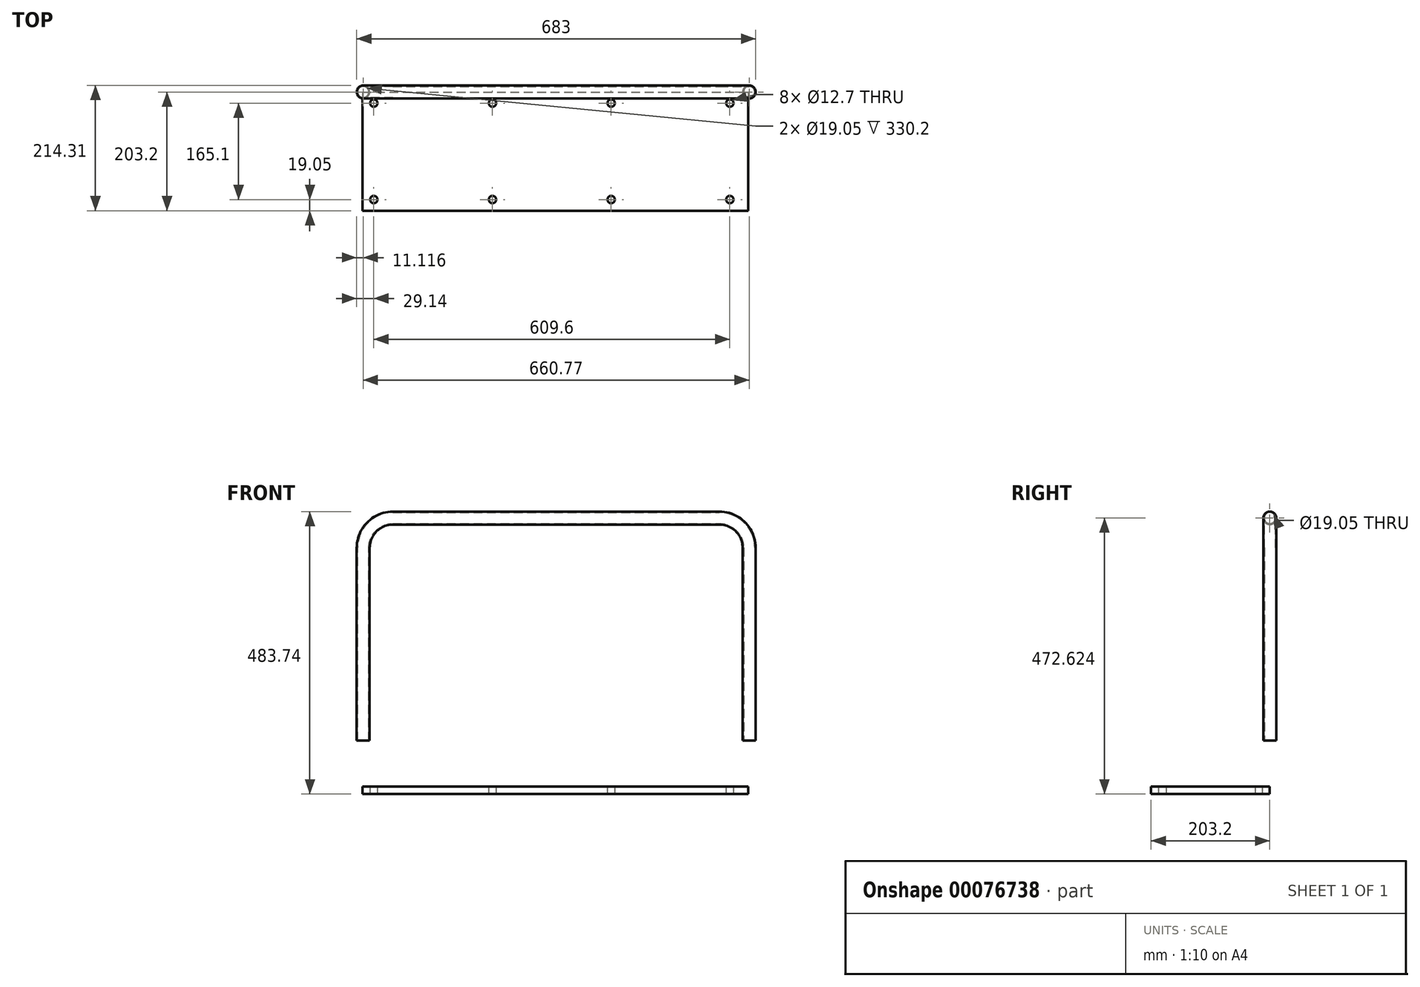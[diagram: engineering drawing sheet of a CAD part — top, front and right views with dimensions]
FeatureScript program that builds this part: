
annotation { "Feature Type Name" : "Feature", "Feature Type Description" : "" }
export const myFeature = defineFeature(function(context is Context, id is Id, definition is map)
    precondition{}
    {
        {
            var Q0;
            Q0=qCreatedBy(makeId("Top.planeOp"),FACE);
            var sketch = newSketch(context, id + "F0", { "sketchPlane" : qUnion([Q0])});
            skLineSegment(sketch, "E0.bottom", {"start": v(-330.2, 0) * mm, "end": v(330.2, 0) * mm});
            skLineSegment(sketch, "E0.top", {"start": v(-330.2, -203.2) * mm, "end": v(330.2, -203.2) * mm});
            skLineSegment(sketch, "E0.left", {"start": v(-330.2, 0) * mm, "end": v(-330.2, -203.2) * mm});
            skLineSegment(sketch, "E0.right", {"start": v(330.2, 0) * mm, "end": v(330.2, -203.2) * mm});
            skSolve(sketch);
        }
        {
            var Q0;
            Q0=makeQuery(id+"F0.imprint","IMPRINT",FACE,{"disambiguationData":[TD([[makeQuery(id+"F0.imprint","IMPRINT",EDGE,{"derivedFrom":sQuery(id+"F0.wireOp",EDGE,"E0.bottom")}),-1.0]])]});
            var sketch = newSketch(context, id + "F1", { "sketchPlane" : qUnion([Q0])});
            skCircle(sketch, "E1", {"center": v(-311.15, -184.15) * mm, "radius": 6.35 * mm});
            skCircle(sketch, "E2.0.1.0", {"center": v(-311.15, -19.05) * mm, "radius": 6.35 * mm});
            skCircle(sketch, "E2.1.0.0", {"center": v(-107.95, -184.15) * mm, "radius": 6.35 * mm});
            skCircle(sketch, "E2.1.1.0", {"center": v(-107.95, -19.05) * mm, "radius": 6.35 * mm});
            skCircle(sketch, "E2.2.0.0", {"center": v(95.25, -184.15) * mm, "radius": 6.35 * mm});
            skCircle(sketch, "E2.2.1.0", {"center": v(95.25, -19.05) * mm, "radius": 6.35 * mm});
            skCircle(sketch, "E2.3.0.0", {"center": v(298.45, -184.15) * mm, "radius": 6.35 * mm});
            skCircle(sketch, "E2.3.1.0", {"center": v(298.45, -19.05) * mm, "radius": 6.35 * mm});
            skLineSegment(sketch, "E2.direction1", {"start": v(-311.15, -184.15) * mm, "end": v(-107.95, -184.15) * mm, "construction": true});
            skLineSegment(sketch, "E2.direction2", {"start": v(-311.15, -184.15) * mm, "end": v(-311.15, -19.05) * mm, "construction": true});
            skSolve(sketch);
        }
        {
            var Q0;
            Q0 = qSketchRegion(id + "F0", true);
            extrude(context, id + "F2", {"entities" : qUnion([Q0]), "depth" : 12.7 * mm});
        }
        {
            var Q0;
            Q0 = qSketchRegion(id + "F1", true);
            extrude(context, id + "F3", {"entities" : qUnion([Q0]), "operationType" : NewBodyOperationType.REMOVE, "endBound" : BoundingType.THROUGH_ALL, "depth" : 25.4 * mm});
        }
        {
            var Q0;
            Q0=qCreatedBy(makeId("Front.planeOp"),FACE);
            var sketch = newSketch(context, id + "F4", { "sketchPlane" : qUnion([Q0])});
            skLineSegment(sketch, "E3", {"start": v(-328.99, 91.44) * mm, "end": v(-328.99, 421.64) * mm});
            skLineSegment(sketch, "E4", {"start": v(-278.19, 472.44) * mm, "end": v(280.61, 472.44) * mm});
            skLineSegment(sketch, "E5", {"start": v(331.41, 421.64) * mm, "end": v(331.41, 91.44) * mm});
            skPoint(sketch, "E6.visualSharp", {"position": v(-328.99, 472.44) * mm});
            skArc(sketch, "E6.filletArc", {"start": v(-278.19, 472.44) * mm, "mid": v(-314.1, 457.56) * mm, "end": v(-328.99, 421.64) * mm});
            skPoint(sketch, "E7.visualSharp", {"position": v(331.41, 472.44) * mm});
            skArc(sketch, "E7.filletArc", {"start": v(331.41, 421.64) * mm, "mid": v(316.53, 457.56) * mm, "end": v(280.61, 472.44) * mm});
            skSolve(sketch);
        }
        {
            var Q0;
            Q0=qCreatedBy(makeId("Top.planeOp"),FACE);
            var Q1;
            Q1=sQuery(id+"F4.wireOp",VERTEX,"E3.start");
            cPlane(context, id + "F5", {"entities" : qUnion([Q0, Q1]), "cplaneType" : CPlaneType.PLANE_POINT, "offset" : 152.4 * mm, "width" : 152.4 * mm, "height" : 152.4 * mm});
        }
        {
            var Q0;
            Q0=qCreatedBy(id+"F5.planeOp",FACE);
            var sketch = newSketch(context, id + "F6", { "sketchPlane" : qUnion([Q0])});
            skCircle(sketch, "E8", {"center": v(-329.17, 0) * mm, "radius": 11.11 * mm});
            skCircle(sketch, "E9", {"center": v(-329.17, 0) * mm, "radius": 9.53 * mm});
            skSolve(sketch);
        }
        {
            var Q0;
            Q0=makeQuery(id+"F6.imprint","IMPRINT",FACE,{"disambiguationData":[TD([[makeQuery(id+"F6.imprint","IMPRINT",EDGE,{"derivedFrom":sQuery(id+"F6.wireOp",EDGE,"E8")}),1.0]])]});
            var Q1;
            Q1=sQuery(id+"F4.wireOp",EDGE,"E3");
            var Q2;
            Q2=sQuery(id+"F4.wireOp",EDGE,"E6.filletArc");
            var Q3;
            Q3=sQuery(id+"F4.wireOp",EDGE,"E4");
            var Q4;
            Q4=sQuery(id+"F4.wireOp",EDGE,"E7.filletArc");
            var Q5;
            Q5=sQuery(id+"F4.wireOp",EDGE,"E5");
            sweep(context, id + "F7", {"profiles" : qUnion([Q0]), "path" : qUnion([Q1, Q2, Q3, Q4, Q5])});
        }
    });
